# Revit family: P201003KC-008c_KMBT5511KSS
name_source: partatom
category: Specialty Equipment
units: mm (PartAtom-declared; Revit-internal decimal feet)

## family parameters
Always vertical = Yes
Cut with Voids When Loaded = No
Enable Cutting in Views = No
Maintain Annotation Orientation = No
Part Type = Normal
Room Calculation Point = No
Round Connector Dimension = Use Diameter
Shared = No
Work Plane-Based = No

## types (1)
- KMBT5511KSS
    Amps = 0 A
    Apparent Load = 0 VA
    Back Panel Material = ARCAT - Metal - Aluminum
    Body Material = ARCAT - Metal - Steel - Black
    Clearance Material = ARCAT - Clearance
    Default Elevation = 0"
    Depth = 18"
    Dimension Guide = https://www.whirlpool.com
    Door Material = ARCAT - Metal - Steel - Stainless
    Family Name = built-in microwave
    Feature 1 = Built-In Low Profile Design
    Feature 2 = Exterior Quick Access Buttons
    Feature 3 = Hidden Microwave Controls
    Glass Material = ARCAT - Glass - Tempered - Gray
    Height = 19 1/8"
    Installation-Fabrication = https://www.whirlpool.com
    Manufacturer = KitchenAid
    Model = KMBT5511KSS
    Switch Material = ARCAT - Metal - Plastic - Grey
    Voltage = 0 V
    Width = 29 3/4"

## geometry (parser evidence)
native form markers: Sweep x3
no freeform markers — native parametric forms only
